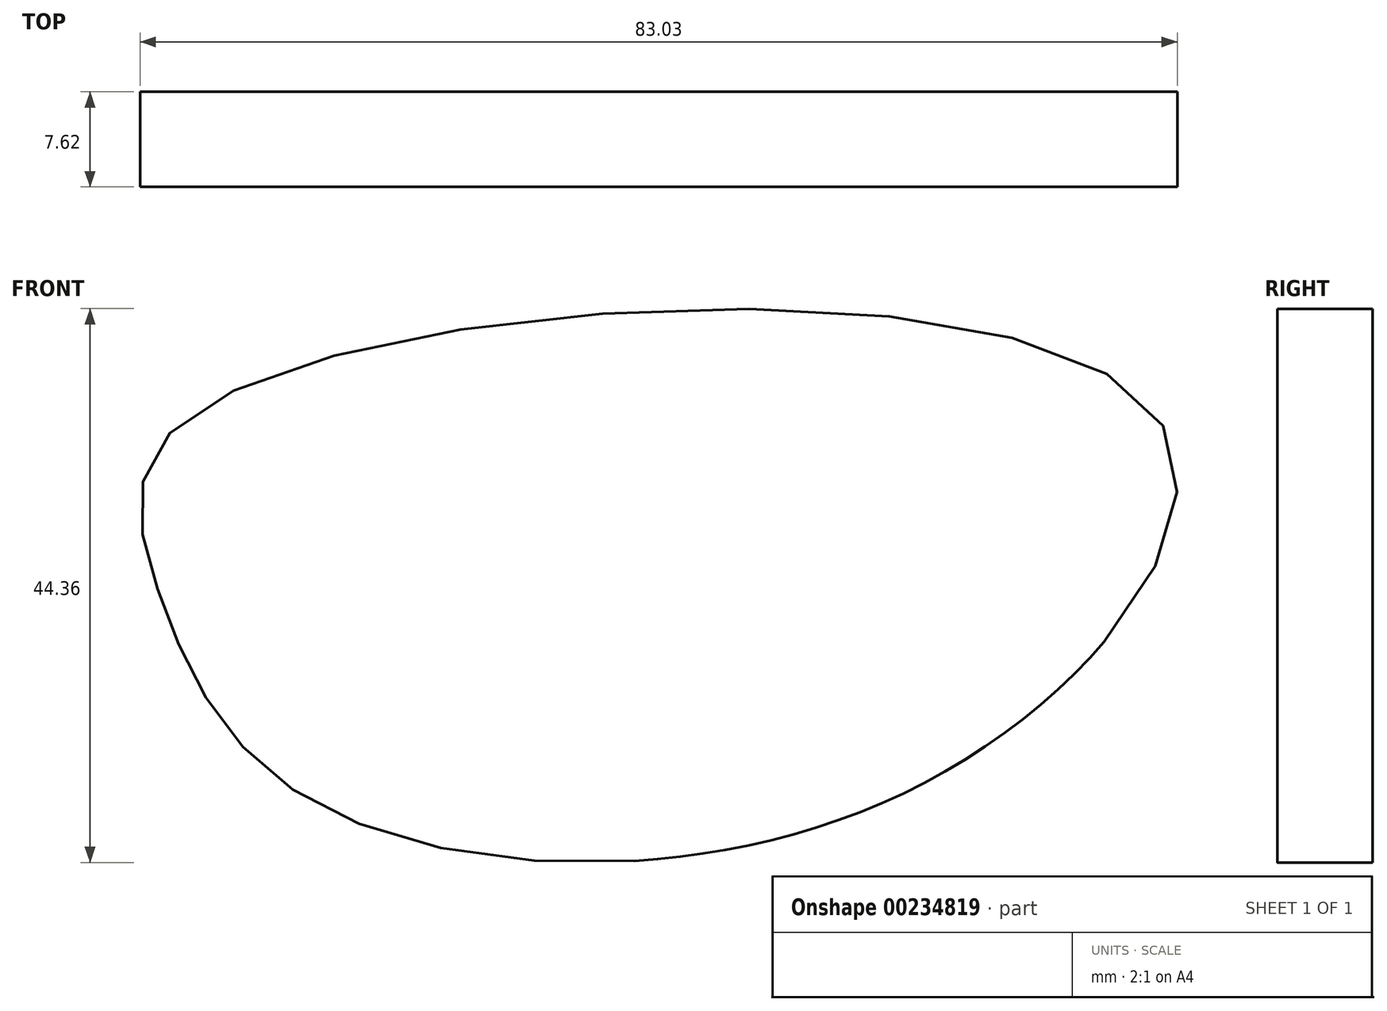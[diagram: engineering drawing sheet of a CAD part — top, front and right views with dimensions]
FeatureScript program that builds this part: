
annotation { "Feature Type Name" : "Feature", "Feature Type Description" : "" }
export const myFeature = defineFeature(function(context is Context, id is Id, definition is map)
    precondition{}
    {
        {
            var Q0;
            Q0=qCreatedBy(makeId("Front.planeOp"),FACE);
            var sketch = newSketch(context, id + "F0", { "sketchPlane" : qUnion([Q0])});
            skFitSpline(sketch, "E0", {"points": [v(-76.1, 38.54) * mm, v(0, 39.24) * mm, v(-16.86, 9.29) * mm, v(-66.43, 7.16) * mm, v(-78.88, 23.71) * mm, v(-76.1, 38.54) * mm]});
            skFitSpline(sketch, "E1", {"points": [v(-36.66, 12.2) * mm, v(39.45, 12.9) * mm, v(22.6, -17.07) * mm, v(-26.98, -19.2) * mm, v(-39.43, -2.64) * mm, v(-36.66, 12.2) * mm]});
            skSolve(sketch);
        }
        {
            var Q0;
            Q0=makeQuery(id+"F0.imprint","IMPRINT",FACE,{"disambiguationData":[TD([[makeQuery(id+"F0.imprint","IMPRINT",EDGE,{"derivedFrom":sQuery(id+"F0.wireOp",EDGE,"E0")}),-1.0]])]});
            extrude(context, id + "F1", {"entities" : qUnion([Q0]), "endBound" : BoundingType.SYMMETRIC, "depth" : 7.62 * mm});
        }
    });
